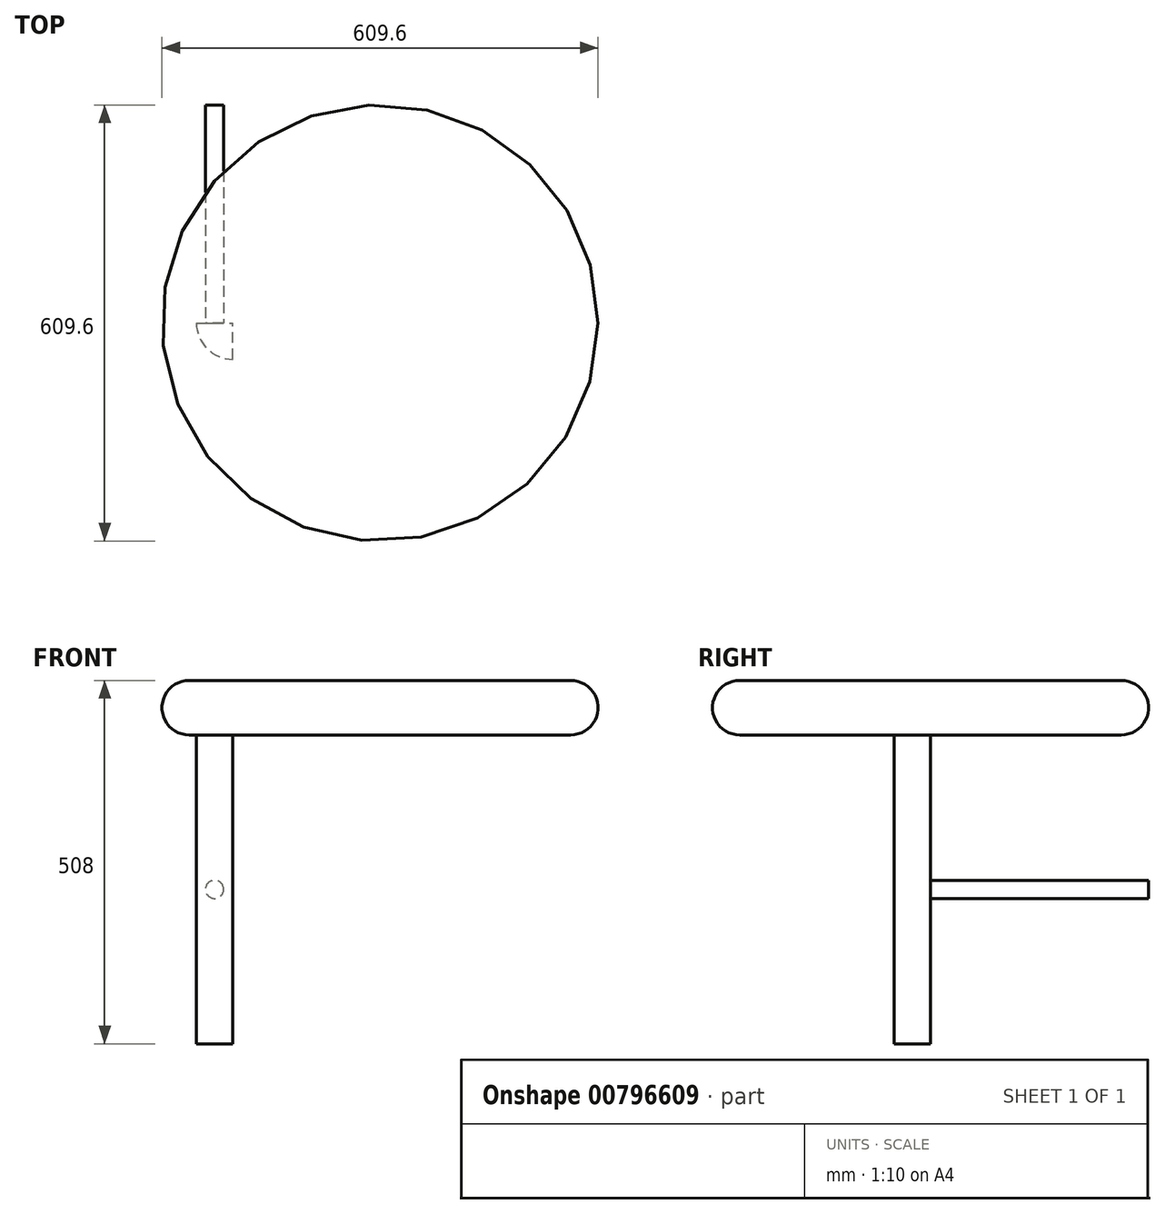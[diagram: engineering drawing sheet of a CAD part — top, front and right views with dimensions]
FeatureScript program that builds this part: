
annotation { "Feature Type Name" : "Feature", "Feature Type Description" : "" }
export const myFeature = defineFeature(function(context is Context, id is Id, definition is map)
    precondition{}
    {
        {
            var Q0;
            Q0=qCreatedBy(makeId("Top.planeOp"),FACE);
            var sketch = newSketch(context, id + "F0", { "sketchPlane" : qUnion([Q0])});
            skCircle(sketch, "E0", {"center": v(0, 0) * mm, "radius": 304.8 * mm});
            skSolve(sketch);
        }
        {
            var Q0;
            Q0 = qSketchRegion(id + "F0", true);
            extrude(context, id + "F1", {"entities" : qUnion([Q0]), "depth" : 76.2 * mm, "offsetDistance" : 25.4 * mm});
        }
        {
            var Q0;
            Q0=makeQuery(id+"F1.opExtrude","CAP_EDGE",EDGE,{"disambiguationData":[OSD([sQuery(id+"F0.wireOp",EDGE,"E0")])],"isStart":false});
            var Q1;
            Q1=makeQuery(id+"F1.opExtrude","CAP_EDGE",EDGE,{"disambiguationData":[OSD([sQuery(id+"F0.wireOp",EDGE,"E0")])],"isStart":true});
            fillet(context, id + "F2", {"entities" : qUnion([Q0, Q1]), "radius" : 38.1 * mm, "tangentPropagation" : true, "allowEdgeOverflow" : false});
        }
        {
            var Q0;
            Q0=qCreatedBy(makeId("Front.planeOp"),FACE);
            var sketch = newSketch(context, id + "F3", { "sketchPlane" : qUnion([Q0])});
            skLineSegment(sketch, "E1.bottom", {"start": v(-256.64, 0) * mm, "end": v(-205.84, 0) * mm});
            skLineSegment(sketch, "E1.top", {"start": v(-256.64, -431.8) * mm, "end": v(-205.84, -431.8) * mm});
            skLineSegment(sketch, "E1.left", {"start": v(-256.64, 0) * mm, "end": v(-256.64, -431.8) * mm});
            skLineSegment(sketch, "E1.right", {"start": v(-205.84, 0) * mm, "end": v(-205.84, -431.8) * mm});
            skSolve(sketch);
        }
        {
            var Q0;
            Q0 = qSketchRegion(id + "F3", true);
            extrude(context, id + "F4", {"entities" : qUnion([Q0]), "depth" : 50.8 * mm, "offsetDistance" : 25.4 * mm});
        }
        {
            var Q0;
            Q0=makeQuery(id+"F4.opExtrude","CAP_EDGE",EDGE,{"disambiguationData":[OSD([sQuery(id+"F3.wireOp",EDGE,"E1.left")])],"isStart":false});
            fillet(context, id + "F5", {"entities" : qUnion([Q0]), "radius" : 50.8 * mm, "tangentPropagation" : true, "allowEdgeOverflow" : false});
        }
        {
            var Q0;
            Q0=makeQuery(id+"F4.opExtrude","CAP_FACE",FACE,{"disambiguationData":[OSD([sQuery(id+"F3.wireOp",EDGE,"E1.bottom"),sQuery(id+"F3.wireOp",EDGE,"E1.top"),sQuery(id+"F3.wireOp",EDGE,"E1.left"),sQuery(id+"F3.wireOp",EDGE,"E1.right")])],"isStart":true});
            var sketch = newSketch(context, id + "F6", { "sketchPlane" : qUnion([Q0])});
            skLineSegment(sketch, "E2", {"start": v(231.24, 0) * mm, "end": v(231.24, -431.8) * mm});
            skCircle(sketch, "E3", {"center": v(231.24, -215.9) * mm, "radius": 12.7 * mm});
            skSolve(sketch);
        }
        {
            var Q0;
            Q0 = qSketchRegion(id + "F6", true);
            extrude(context, id + "F7", {"entities" : qUnion([Q0]), "operationType" : NewBodyOperationType.ADD, "depth" : 304.8 * mm, "offsetDistance" : 25.4 * mm});
        }
    });
